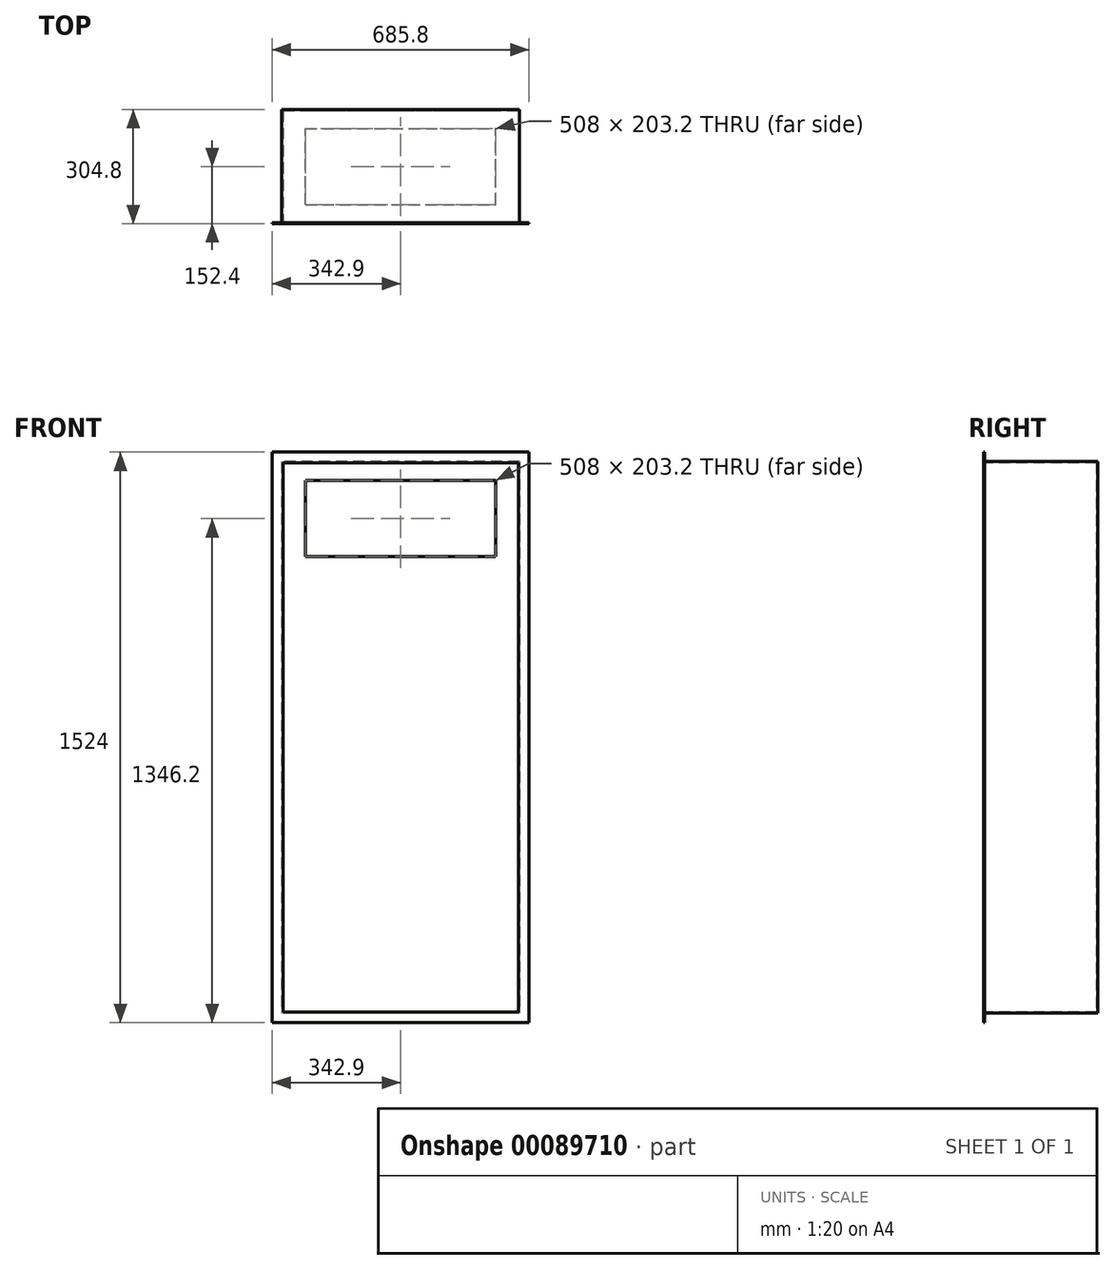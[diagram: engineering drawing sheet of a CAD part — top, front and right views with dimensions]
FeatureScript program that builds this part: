
annotation { "Feature Type Name" : "Feature", "Feature Type Description" : "" }
export const myFeature = defineFeature(function(context is Context, id is Id, definition is map)
    precondition{}
    {
        {
            var Q0;
            Q0=qCreatedBy(makeId("Right.planeOp"),FACE);
            var sketch = newSketch(context, id + "F0", { "sketchPlane" : qUnion([Q0])});
            skLineSegment(sketch, "E0.bottom", {"start": v(152.4, 736.6) * mm, "end": v(-152.4, 736.6) * mm});
            skLineSegment(sketch, "E0.top", {"start": v(152.4, -736.6) * mm, "end": v(-152.4, -736.6) * mm});
            skLineSegment(sketch, "E0.left", {"start": v(152.4, 736.6) * mm, "end": v(152.4, -736.6) * mm});
            skLineSegment(sketch, "E0.right", {"start": v(-152.4, 736.6) * mm, "end": v(-152.4, -736.6) * mm});
            skPoint(sketch, "E0.middle", {"position": v(0, 0) * mm});
            skSolve(sketch);
        }
        {
            var Q0;
            Q0 = qSketchRegion(id + "F0", true);
            extrude(context, id + "F1", {"entities" : qUnion([Q0]), "endBound" : BoundingType.SYMMETRIC, "depth" : 635 * mm});
        }
        {
            var Q0;
            Q0=makeQuery(id+"F1.opExtrude","SWEPT_FACE",FACE,{"disambiguationData":[OSD([sQuery(id+"F0.wireOp",EDGE,"E0.right")])]});
            shell(context, id + "F2", {"entities" : qUnion([Q0]), "thickness" : 3.17 * mm});
        }
        {
            var Q0;
            Q0=makeQuery(id+"F1.opExtrude","SWEPT_FACE",FACE,{"disambiguationData":[OSD([sQuery(id+"F0.wireOp",EDGE,"E0.right")])]});
            var sketch = newSketch(context, id + "F3", { "sketchPlane" : qUnion([Q0])});
            skLineSegment(sketch, "E1.top", {"start": v(-314.33, -733.43) * mm, "end": v(314.33, -733.43) * mm});
            skLineSegment(sketch, "E1.left", {"start": v(-314.33, 733.42) * mm, "end": v(-314.33, -733.43) * mm});
            skLineSegment(sketch, "E1.right", {"start": v(314.32, 733.42) * mm, "end": v(314.33, -733.43) * mm});
            skLineSegment(sketch, "E2.bottom", {"start": v(342.9, -762) * mm, "end": v(-342.9, -762) * mm});
            skLineSegment(sketch, "E2.left", {"start": v(342.9, -762) * mm, "end": v(342.9, 762) * mm});
            skLineSegment(sketch, "E2.right", {"start": v(-342.9, -762) * mm, "end": v(-342.9, 762) * mm});
            skLineSegment(sketch, "E3", {"start": v(-314.33, 733.42) * mm, "end": v(314.32, 733.42) * mm});
            skLineSegment(sketch, "E4", {"start": v(-342.9, 762) * mm, "end": v(342.9, 762) * mm});
            skSolve(sketch);
        }
        {
            var Q0;
            Q0 = qSketchRegion(id + "F3", true);
            extrude(context, id + "F4", {"entities" : qUnion([Q0]), "operationType" : NewBodyOperationType.ADD, "oppositeDirection" : true, "depth" : 3.17 * mm});
        }
        {
            var Q0;
            Q0=makeQuery(id+"F1.opExtrude","SWEPT_FACE",FACE,{"disambiguationData":[OSD([sQuery(id+"F0.wireOp",EDGE,"E0.left")])]});
            var sketch = newSketch(context, id + "F5", { "sketchPlane" : qUnion([Q0])});
            skLineSegment(sketch, "E5.bottom", {"start": v(-254, 685.8) * mm, "end": v(254, 685.8) * mm});
            skLineSegment(sketch, "E5.top", {"start": v(-254, 482.6) * mm, "end": v(254, 482.6) * mm});
            skLineSegment(sketch, "E5.left", {"start": v(-254, 685.8) * mm, "end": v(-254, 482.6) * mm});
            skLineSegment(sketch, "E5.right", {"start": v(254, 685.8) * mm, "end": v(254, 482.6) * mm});
            skLineSegment(sketch, "E6", {"start": v(-254, 482.6) * mm, "end": v(254, 685.8) * mm, "construction": true});
            skLineSegment(sketch, "E7", {"start": v(254, 482.6) * mm, "end": v(-254, 685.8) * mm, "construction": true});
            skPoint(sketch, "E8", {"position": v(0, 584.2) * mm});
            skSolve(sketch);
        }
        {
            var Q0;
            Q0 = qSketchRegion(id + "F5", true);
            extrude(context, id + "F6", {"entities" : qUnion([Q0]), "operationType" : NewBodyOperationType.REMOVE, "endBound" : BoundingType.THROUGH_ALL, "oppositeDirection" : true, "depth" : 25.4 * mm});
        }
        {
            var Q0;
            Q0=makeQuery(id+"F1.opExtrude","SWEPT_FACE",FACE,{"disambiguationData":[OSD([sQuery(id+"F0.wireOp",EDGE,"E0.top")])]});
            var sketch = newSketch(context, id + "F7", { "sketchPlane" : qUnion([Q0])});
            skLineSegment(sketch, "E9.bottom", {"start": v(254, -101.6) * mm, "end": v(-254, -101.6) * mm});
            skLineSegment(sketch, "E9.top", {"start": v(254, 101.6) * mm, "end": v(-254, 101.6) * mm});
            skLineSegment(sketch, "E9.left", {"start": v(254, -101.6) * mm, "end": v(254, 101.6) * mm});
            skLineSegment(sketch, "E9.right", {"start": v(-254, -101.6) * mm, "end": v(-254, 101.6) * mm});
            skPoint(sketch, "E9.middle", {"position": v(0, 0) * mm});
            skSolve(sketch);
        }
        {
            var Q0;
            Q0 = qSketchRegion(id + "F7", true);
            extrude(context, id + "F8", {"entities" : qUnion([Q0]), "operationType" : NewBodyOperationType.REMOVE, "endBound" : BoundingType.UP_TO_NEXT, "oppositeDirection" : true, "depth" : 25.4 * mm});
        }
    });
